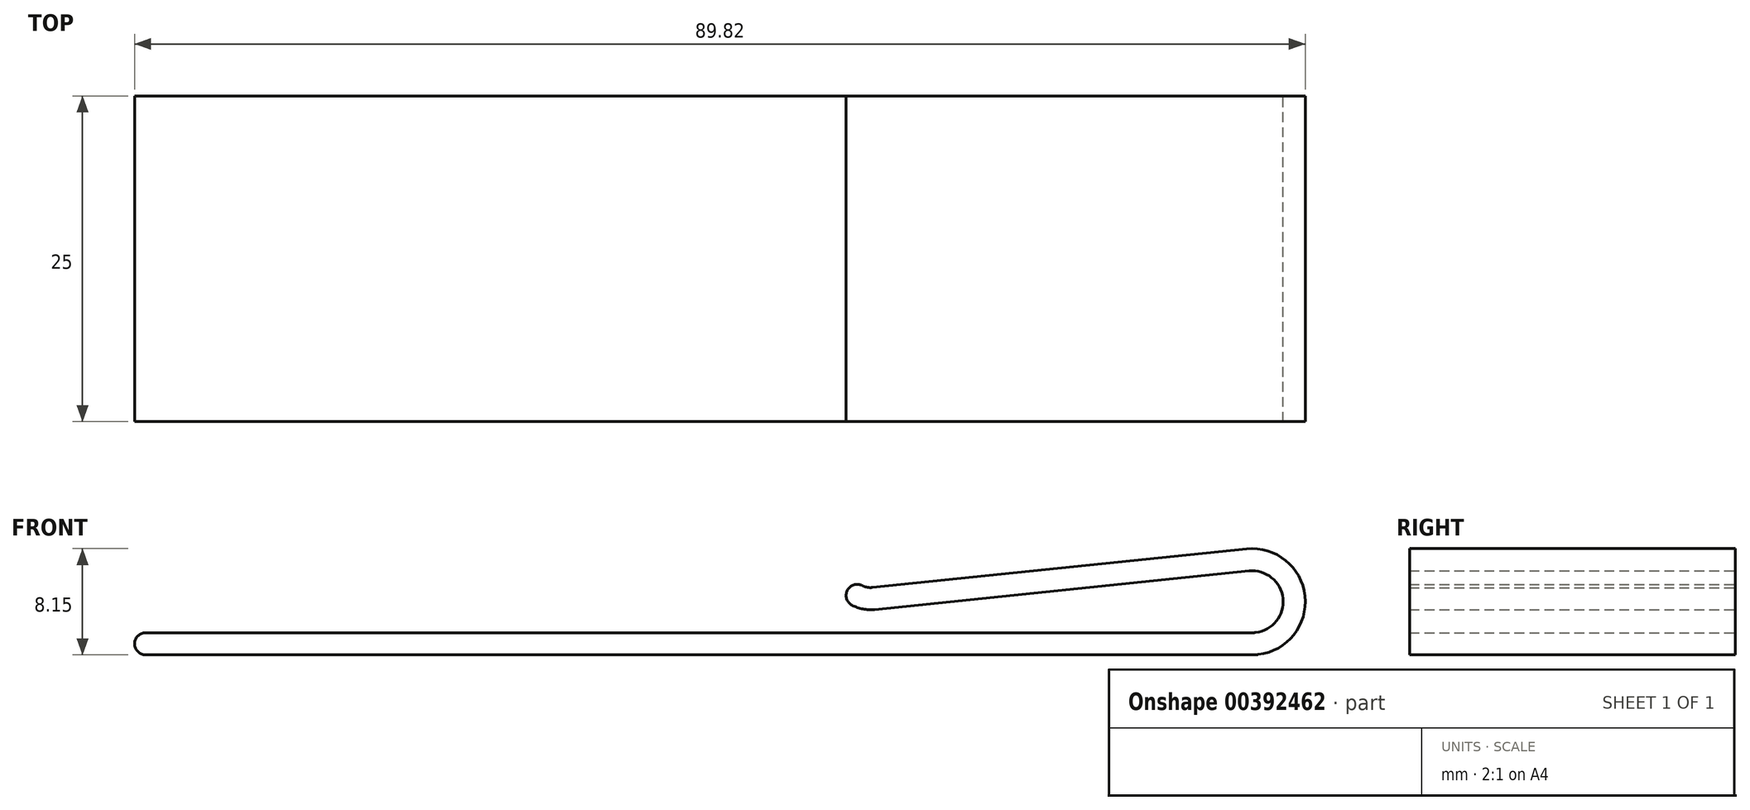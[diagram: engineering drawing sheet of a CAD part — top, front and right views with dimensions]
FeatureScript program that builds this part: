
annotation { "Feature Type Name" : "Feature", "Feature Type Description" : "" }
export const myFeature = defineFeature(function(context is Context, id is Id, definition is map)
    precondition{}
    {
        {
            var Q0;
            Q0=qCreatedBy(makeId("Front.planeOp"),FACE);
            var sketch = newSketch(context, id + "F0", { "sketchPlane" : qUnion([Q0])});
            skLineSegment(sketch, "E0", {"start": v(-39.15, 23.39) * mm, "end": v(45.79, 23.39) * mm});
            skLineSegment(sketch, "E1", {"start": v(16.78, 25.17) * mm, "end": v(45.5, 28.13) * mm});
            skArc(sketch, "E2", {"start": v(46.02, 23.4) * mm, "mid": v(48.1, 26.02) * mm, "end": v(45.5, 28.13) * mm});
            skPoint(sketch, "E3.visualSharp", {"position": v(45.85, 23.39) * mm});
            skArc(sketch, "E3.filletArc", {"start": v(45.79, 23.39) * mm, "mid": v(45.9, 23.4) * mm, "end": v(46.02, 23.4) * mm});
            skArc(sketch, "E4", {"start": v(15.04, 25.5) * mm, "mid": v(15.88, 25.2) * mm, "end": v(16.78, 25.17) * mm});
            skArc(sketch, "E5.0", {"start": v(15.83, 27) * mm, "mid": v(16.2, 26.87) * mm, "end": v(16.6, 26.86) * mm});
            skLineSegment(sketch, "E5.1", {"start": v(-39.15, 21.69) * mm, "end": v(45.79, 21.69) * mm});
            skArc(sketch, "E5.2", {"start": v(45.79, 21.69) * mm, "mid": v(46, 21.7) * mm, "end": v(46.22, 21.71) * mm});
            skArc(sketch, "E5.3", {"start": v(46.22, 21.71) * mm, "mid": v(49.8, 26.2) * mm, "end": v(45.32, 29.82) * mm});
            skLineSegment(sketch, "E5.4", {"start": v(16.6, 26.86) * mm, "end": v(45.32, 29.82) * mm});
            skArc(sketch, "E6", {"start": v(15.83, 27) * mm, "mid": v(14.68, 26.64) * mm, "end": v(15.04, 25.5) * mm});
            skArc(sketch, "E7", {"start": v(-39.15, 23.39) * mm, "mid": v(-40, 22.54) * mm, "end": v(-39.15, 21.69) * mm});
            skSolve(sketch);
        }
        {
            var Q0;
            Q0 = qSketchRegion(id + "F0", true);
            extrude(context, id + "F1", {"entities" : qUnion([Q0]), "depth" : 25 * mm});
        }
        {
            var Q0;
            Q0=makeQuery(id+"F1.opExtrude","SWEPT_FACE",FACE,{"disambiguationData":[OSD([sQuery(id+"F0.wireOp",EDGE,"E5.1")])]});
            var sketch = newSketch(context, id + "F2", { "sketchPlane" : qUnion([Q0])});
            skText(sketch, "E8", { "text": "H", "fontName": "OpenSans-Regular.ttf"});
            const initialGuessF2  = {"E8": [0.02773, 0.04246, 1, 0, 0.01245]};
            skSetInitialGuess(sketch, initialGuessF2);
            skSolve(sketch);
        }
    });
